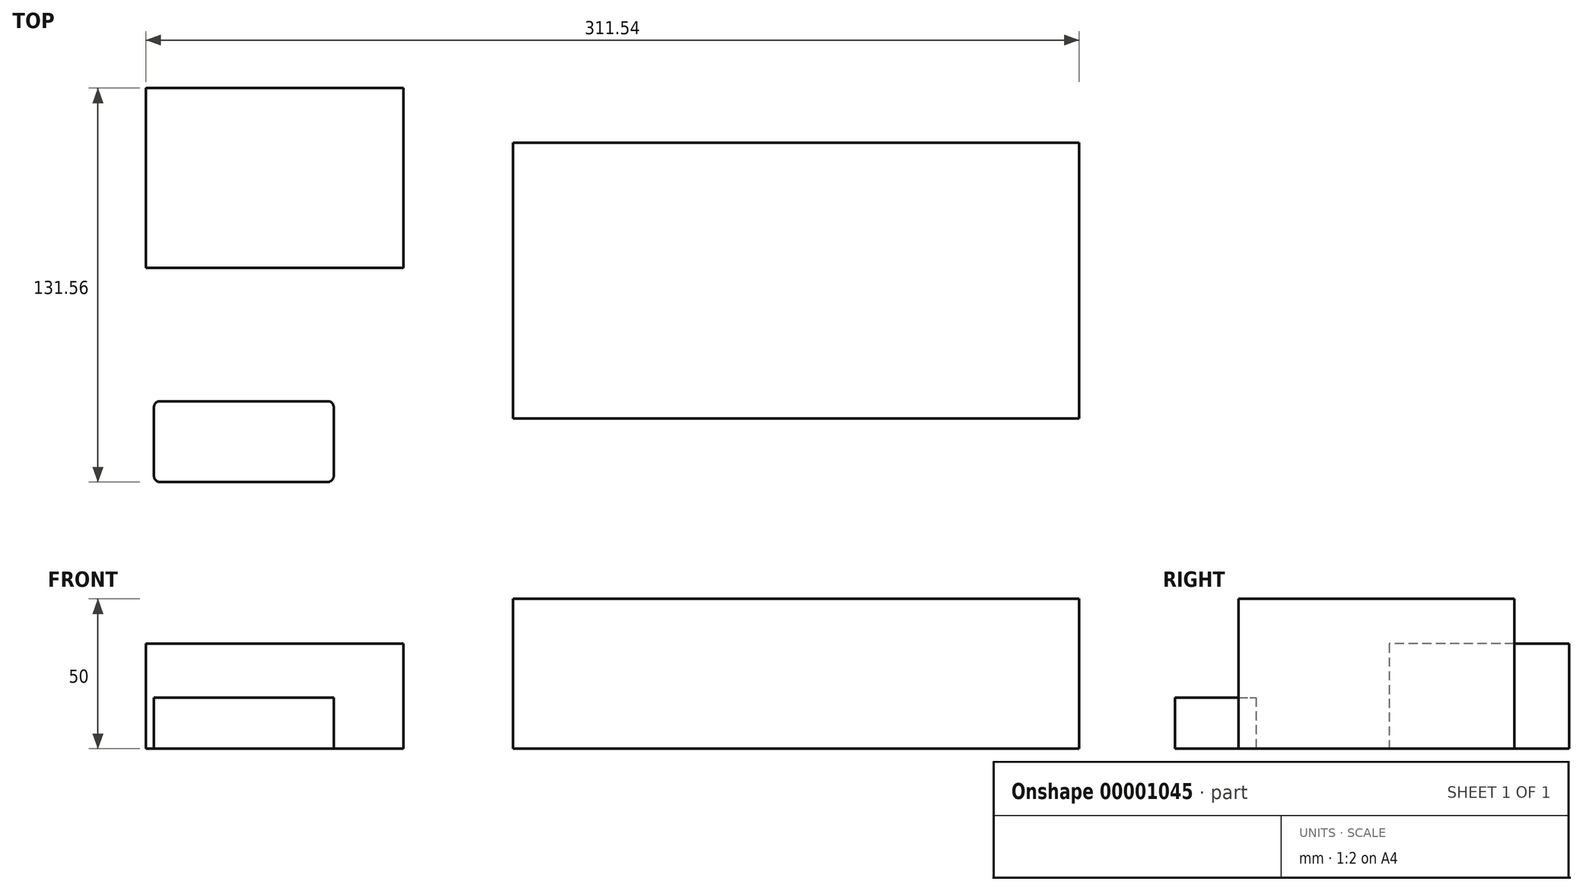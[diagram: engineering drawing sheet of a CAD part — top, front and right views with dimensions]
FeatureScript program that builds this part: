
annotation { "Feature Type Name" : "Feature", "Feature Type Description" : "" }
export const myFeature = defineFeature(function(context is Context, id is Id, definition is map)
    precondition{}
    {
        {
            var Q0;
            Q0=qCreatedBy(makeId("Top.planeOp"),FACE);
            var sketch = newSketch(context, id + "F0", { "sketchPlane" : qUnion([Q0])});
            skLineSegment(sketch, "E0.bottom", {"start": v(-119.1, 93.03) * mm, "end": v(-33.1, 93.03) * mm});
            skLineSegment(sketch, "E0.top", {"start": v(-119.1, 33.03) * mm, "end": v(-33.1, 33.03) * mm});
            skLineSegment(sketch, "E0.left", {"start": v(-119.1, 93.03) * mm, "end": v(-119.1, 33.03) * mm});
            skLineSegment(sketch, "E0.right", {"start": v(-33.1, 93.03) * mm, "end": v(-33.1, 33.03) * mm});
            skSolve(sketch);
        }
        {
            var Q0;
            Q0=makeQuery(id+"F0.imprint","IMPRINT",FACE,{"disambiguationData":[TD([[makeQuery(id+"F0.imprint","IMPRINT",EDGE,{"derivedFrom":sQuery(id+"F0.wireOp",EDGE,"E0.bottom")}),-1.0]])]});
            extrude(context, id + "F1", {"entities" : qUnion([Q0]), "depth" : 35 * mm, "offsetDistance" : 25 * mm});
        }
        {
            var Q0;
            Q0=qCreatedBy(makeId("Top.planeOp"),FACE);
            var sketch = newSketch(context, id + "F2", { "sketchPlane" : qUnion([Q0])});
            skLineSegment(sketch, "E1.bottom", {"start": v(192.45, -17.28) * mm, "end": v(3.45, -17.28) * mm});
            skLineSegment(sketch, "E1.top", {"start": v(192.45, 74.72) * mm, "end": v(3.45, 74.72) * mm});
            skLineSegment(sketch, "E1.left", {"start": v(192.45, -17.28) * mm, "end": v(192.45, 74.72) * mm});
            skLineSegment(sketch, "E1.right", {"start": v(3.45, -17.28) * mm, "end": v(3.45, 74.72) * mm});
            skSolve(sketch);
        }
        {
            var Q0;
            Q0=makeQuery(id+"F2.imprint","IMPRINT",FACE,{"disambiguationData":[TD([[makeQuery(id+"F2.imprint","IMPRINT",EDGE,{"derivedFrom":sQuery(id+"F2.wireOp",EDGE,"E1.bottom")}),-1.0]])]});
            extrude(context, id + "F3", {"entities" : qUnion([Q0]), "depth" : 50 * mm, "offsetDistance" : 25 * mm});
        }
        {
            var Q0;
            Q0=qCreatedBy(makeId("Top.planeOp"),FACE);
            var sketch = newSketch(context, id + "F4", { "sketchPlane" : qUnion([Q0])});
            skLineSegment(sketch, "E2.bottom", {"start": v(-56.4, -38.53) * mm, "end": v(-116.4, -38.53) * mm});
            skLineSegment(sketch, "E2.top", {"start": v(-56.4, -11.53) * mm, "end": v(-116.4, -11.53) * mm});
            skLineSegment(sketch, "E2.left", {"start": v(-56.4, -38.53) * mm, "end": v(-56.4, -11.53) * mm});
            skLineSegment(sketch, "E2.right", {"start": v(-116.4, -38.53) * mm, "end": v(-116.4, -11.53) * mm});
            skSolve(sketch);
        }
        {
            var Q0;
            Q0=makeQuery(id+"F4.imprint","IMPRINT",FACE,{"disambiguationData":[TD([[makeQuery(id+"F4.imprint","IMPRINT",EDGE,{"derivedFrom":sQuery(id+"F4.wireOp",EDGE,"E2.bottom")}),-1.0]])]});
            extrude(context, id + "F5", {"entities" : qUnion([Q0]), "depth" : 17 * mm, "offsetDistance" : 25 * mm});
        }
        {
            var Q0;
            Q0=makeQuery(id+"F5.opExtrude","SWEPT_EDGE",EDGE,{"disambiguationData":[OSD([sQuery(id+"F4.wireOp",EDGE,"E2.top"),sQuery(id+"F4.wireOp",EDGE,"E2.right")])]});
            var Q1;
            Q1=makeQuery(id+"F5.opExtrude","SWEPT_EDGE",EDGE,{"disambiguationData":[OSD([sQuery(id+"F4.wireOp",EDGE,"E2.bottom"),sQuery(id+"F4.wireOp",EDGE,"E2.right")])]});
            var Q2;
            Q2=makeQuery(id+"F5.opExtrude","SWEPT_EDGE",EDGE,{"disambiguationData":[OSD([sQuery(id+"F4.wireOp",EDGE,"E2.top"),sQuery(id+"F4.wireOp",EDGE,"E2.left")])]});
            var Q3;
            Q3=makeQuery(id+"F5.opExtrude","SWEPT_EDGE",EDGE,{"disambiguationData":[OSD([sQuery(id+"F4.wireOp",EDGE,"E2.bottom"),sQuery(id+"F4.wireOp",EDGE,"E2.left")])]});
            fillet(context, id + "F6", {"entities" : qUnion([Q0, Q1, Q2, Q3]), "radius" : 2 * mm, "tangentPropagation" : true, "allowEdgeOverflow" : false});
        }
    });
